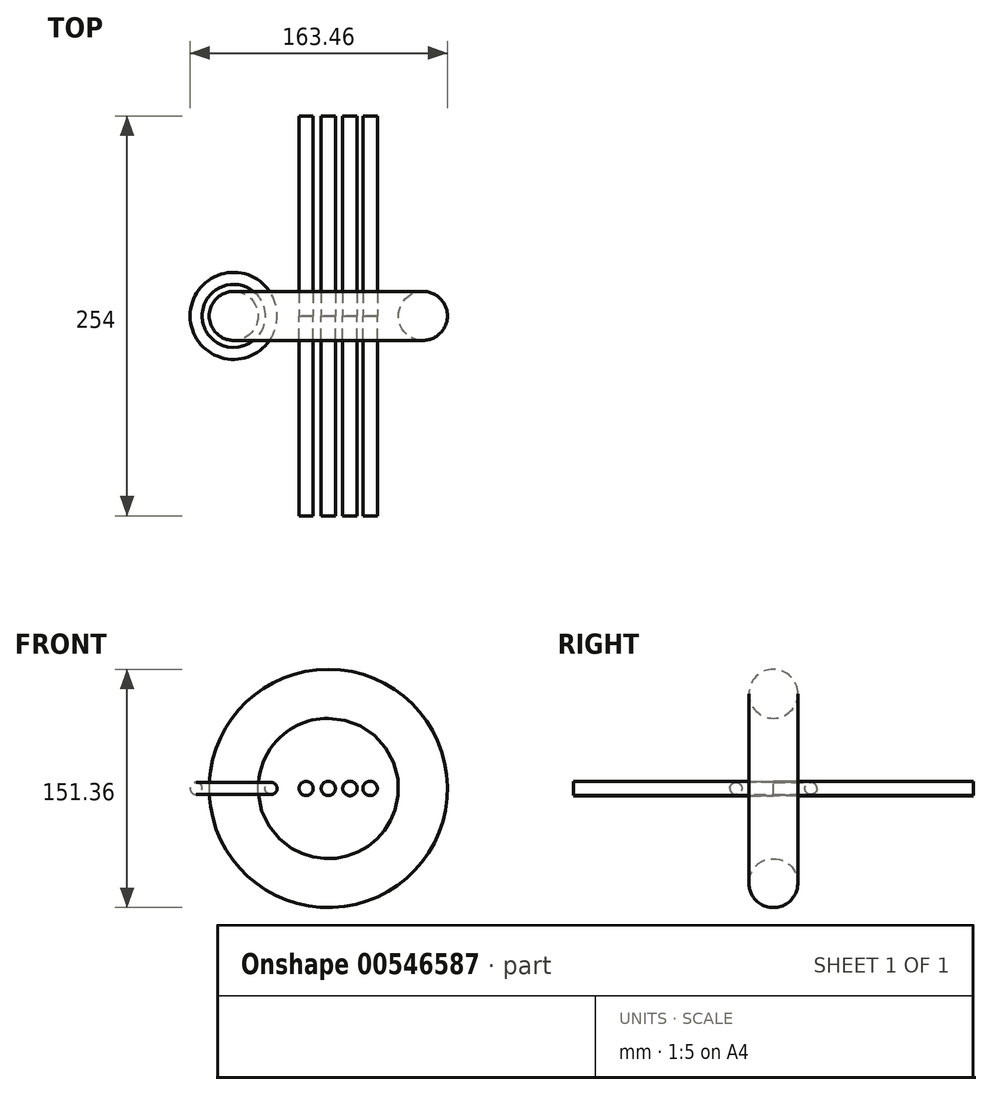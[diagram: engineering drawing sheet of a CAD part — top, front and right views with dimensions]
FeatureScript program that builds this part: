
annotation { "Feature Type Name" : "Feature", "Feature Type Description" : "" }
export const myFeature = defineFeature(function(context is Context, id is Id, definition is map)
    precondition{}
    {
        {
            var Q0;
            Q0=qCreatedBy(makeId("Front.planeOp"),FACE);
            var sketch = newSketch(context, id + "F0", { "sketchPlane" : qUnion([Q0])});
            skCircle(sketch, "E0", {"center": v(0, 0) * mm, "radius": 59.9 * mm});
            skSolve(sketch);
        }
        {
            var Q0;
            Q0=qCreatedBy(makeId("Top.planeOp"),FACE);
            var sketch = newSketch(context, id + "F1", { "sketchPlane" : qUnion([Q0])});
            skCircle(sketch, "E1", {"center": v(-60.14, 0) * mm, "radius": 15.55 * mm});
            skCircle(sketch, "E2", {"center": v(-60.14, 0) * mm, "radius": 24.06 * mm});
            skSolve(sketch);
        }
        {
            var Q0;
            Q0=makeQuery(id+"F1.imprint","IMPRINT",FACE,{"disambiguationData":[TD([[makeQuery(id+"F1.imprint","IMPRINT",EDGE,{"derivedFrom":sQuery(id+"F1.wireOp",EDGE,"E1")}),1.0]])]});
            var Q1;
            Q1=sQuery(id+"F0.wireOp",EDGE,"E0");
            revolve(context, id + "F2", {"entities" : qUnion([Q0]), "axis" : qUnion([Q1]), "revolveType" : RevolveType.FULL});
        }
        {
            var Q0;
            Q0=qCreatedBy(makeId("Front.planeOp"),FACE);
            var sketch = newSketch(context, id + "F3", { "sketchPlane" : qUnion([Q0])});
            skCircle(sketch, "E3", {"center": v(-36.32, 0) * mm, "radius": 3.82 * mm});
            skCircle(sketch, "E4", {"center": v(0, 0) * mm, "radius": 4.51 * mm});
            skCircle(sketch, "E5", {"center": v(13.77, 0) * mm, "radius": 4.62 * mm});
            skCircle(sketch, "E6", {"center": v(-14.04, 0) * mm, "radius": 4.5 * mm});
            skCircle(sketch, "E7", {"center": v(26.57, 0) * mm, "radius": 4.58 * mm});
            skSolve(sketch);
        }
        {
            var Q0;
            Q0=makeQuery(id+"F3.imprint","IMPRINT",FACE,{"disambiguationData":[TD([[makeQuery(id+"F3.imprint","IMPRINT",EDGE,{"derivedFrom":sQuery(id+"F3.wireOp",EDGE,"E3")}),1.0]])]});
            var Q1;
            Q1=sQuery(id+"F1.wireOp",EDGE,"E2");
            revolve(context, id + "F4", {"entities" : qUnion([Q0]), "axis" : qUnion([Q1]), "revolveType" : RevolveType.FULL});
        }
        {
            var Q0;
            Q0=makeQuery(id+"F3.imprint","IMPRINT",FACE,{"disambiguationData":[TD([[makeQuery(id+"F3.imprint","IMPRINT",EDGE,{"derivedFrom":sQuery(id+"F3.wireOp",EDGE,"E6")}),1.0]])]});
            var Q1;
            Q1=makeQuery(id+"F3.imprint","IMPRINT",FACE,{"disambiguationData":[TD([[makeQuery(id+"F3.imprint","IMPRINT",EDGE,{"derivedFrom":sQuery(id+"F3.wireOp",EDGE,"E4")}),1.0]])]});
            var Q2;
            Q2=makeQuery(id+"F3.imprint","IMPRINT",FACE,{"disambiguationData":[TD([[makeQuery(id+"F3.imprint","IMPRINT",EDGE,{"derivedFrom":sQuery(id+"F3.wireOp",EDGE,"E5")}),1.0]])]});
            var Q3;
            Q3=makeQuery(id+"F3.imprint","IMPRINT",FACE,{"disambiguationData":[TD([[makeQuery(id+"F3.imprint","IMPRINT",EDGE,{"derivedFrom":sQuery(id+"F3.wireOp",EDGE,"E7")}),1.0]])]});
            extrude(context, id + "F5", {"entities" : qUnion([Q0, Q1, Q2, Q3]), "depth" : 127 * mm, "offsetDistance" : 25.4 * mm});
        }
        {
            var Q0;
            Q0=makeQuery(id+"F3.imprint","IMPRINT",FACE,{"disambiguationData":[TD([[makeQuery(id+"F3.imprint","IMPRINT",EDGE,{"derivedFrom":sQuery(id+"F3.wireOp",EDGE,"E6")}),1.0]])]});
            var Q1;
            Q1=makeQuery(id+"F3.imprint","IMPRINT",FACE,{"disambiguationData":[TD([[makeQuery(id+"F3.imprint","IMPRINT",EDGE,{"derivedFrom":sQuery(id+"F3.wireOp",EDGE,"E4")}),1.0]])]});
            var Q2;
            Q2=makeQuery(id+"F3.imprint","IMPRINT",FACE,{"disambiguationData":[TD([[makeQuery(id+"F3.imprint","IMPRINT",EDGE,{"derivedFrom":sQuery(id+"F3.wireOp",EDGE,"E5")}),1.0]])]});
            var Q3;
            Q3=makeQuery(id+"F3.imprint","IMPRINT",FACE,{"disambiguationData":[TD([[makeQuery(id+"F3.imprint","IMPRINT",EDGE,{"derivedFrom":sQuery(id+"F3.wireOp",EDGE,"E7")}),1.0]])]});
            extrude(context, id + "F6", {"entities" : qUnion([Q0, Q1, Q2, Q3]), "oppositeDirection" : true, "depth" : 127 * mm, "offsetDistance" : 25.4 * mm});
        }
    });
